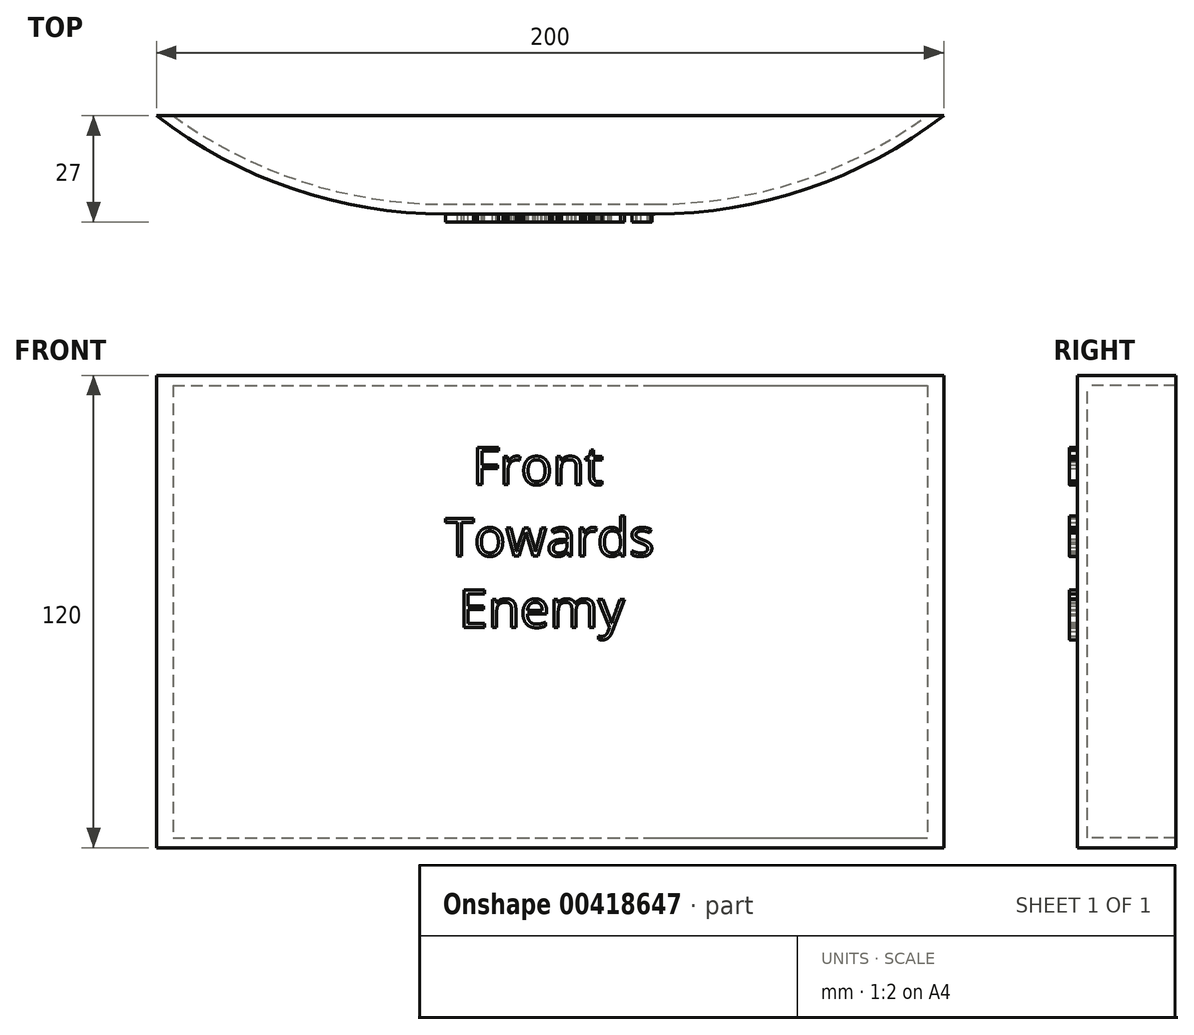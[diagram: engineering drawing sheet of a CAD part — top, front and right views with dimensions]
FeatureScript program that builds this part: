
annotation { "Feature Type Name" : "Feature", "Feature Type Description" : "" }
export const myFeature = defineFeature(function(context is Context, id is Id, definition is map)
    precondition{}
    {
        {
            var Q0;
            Q0=qCreatedBy(makeId("Front.planeOp"),FACE);
            var sketch = newSketch(context, id + "F0", { "sketchPlane" : qUnion([Q0])});
            skLineSegment(sketch, "E0.bottom", {"start": v(-95.66, 35.85) * mm, "end": v(104.34, 35.85) * mm});
            skLineSegment(sketch, "E0.top", {"start": v(-95.66, -84.15) * mm, "end": v(104.34, -84.15) * mm});
            skLineSegment(sketch, "E0.left", {"start": v(-95.66, 35.85) * mm, "end": v(-95.66, -84.15) * mm});
            skLineSegment(sketch, "E0.right", {"start": v(104.34, 35.85) * mm, "end": v(104.34, -84.15) * mm});
            skSolve(sketch);
        }
        {
            var Q0;
            Q0 = qSketchRegion(id + "F0", true);
            extrude(context, id + "F1", {"entities" : qUnion([Q0]), "depth" : 25 * mm});
        }
        {
            var Q0;
            Q0=makeQuery(id+"F1.opExtrude","CAP_EDGE",EDGE,{"disambiguationData":[OSD([sQuery(id+"F0.wireOp",EDGE,"E0.left")])],"isStart":false});
            var Q1;
            Q1=makeQuery(id+"F1.opExtrude","CAP_EDGE",EDGE,{"disambiguationData":[OSD([sQuery(id+"F0.wireOp",EDGE,"E0.right")])],"isStart":false});
            fillet(context, id + "F2", {"entities" : qUnion([Q0, Q1]), "radius" : 120 * mm, "tangentPropagation" : true, "allowEdgeOverflow" : false});
        }
        {
            var Q0;
            Q0=makeQuery(id+"F1.opExtrude","CAP_FACE",FACE,{"disambiguationData":[OSD([sQuery(id+"F0.wireOp",EDGE,"E0.bottom"),sQuery(id+"F0.wireOp",EDGE,"E0.top"),sQuery(id+"F0.wireOp",EDGE,"E0.left"),sQuery(id+"F0.wireOp",EDGE,"E0.right")])],"isStart":true});
            shell(context, id + "F3", {"entities" : qUnion([Q0]), "thickness" : 2.5 * mm});
        }
        {
            var Q0;
            Q0=makeQuery(id+"F1.opExtrude","CAP_FACE",FACE,{"disambiguationData":[OSD([sQuery(id+"F0.wireOp",EDGE,"E0.bottom"),sQuery(id+"F0.wireOp",EDGE,"E0.top"),sQuery(id+"F0.wireOp",EDGE,"E0.left"),sQuery(id+"F0.wireOp",EDGE,"E0.right")])],"isStart":false});
            var sketch = newSketch(context, id + "F4", { "sketchPlane" : qUnion([Q0])});
            skText(sketch, "E1", { "text": "  Front\nTowards\n Enemy", "fontName": "OpenSans-Regular.ttf"});
            const initialGuessF4  = {"E1": [-0.02234, 0.0081, 1, 0, 0.00959]};
            skSetInitialGuess(sketch, initialGuessF4);
            skSolve(sketch);
        }
        {
            var Q0;
            Q0 = qSketchRegion(id + "F4", true);
            extrude(context, id + "F5", {"entities" : qUnion([Q0]), "operationType" : NewBodyOperationType.ADD, "depth" : 2 * mm, "hasSecondDirection" : true, "secondDirectionOppositeDirection" : true, "secondDirectionDepth" : 2 * mm});
        }
    });
